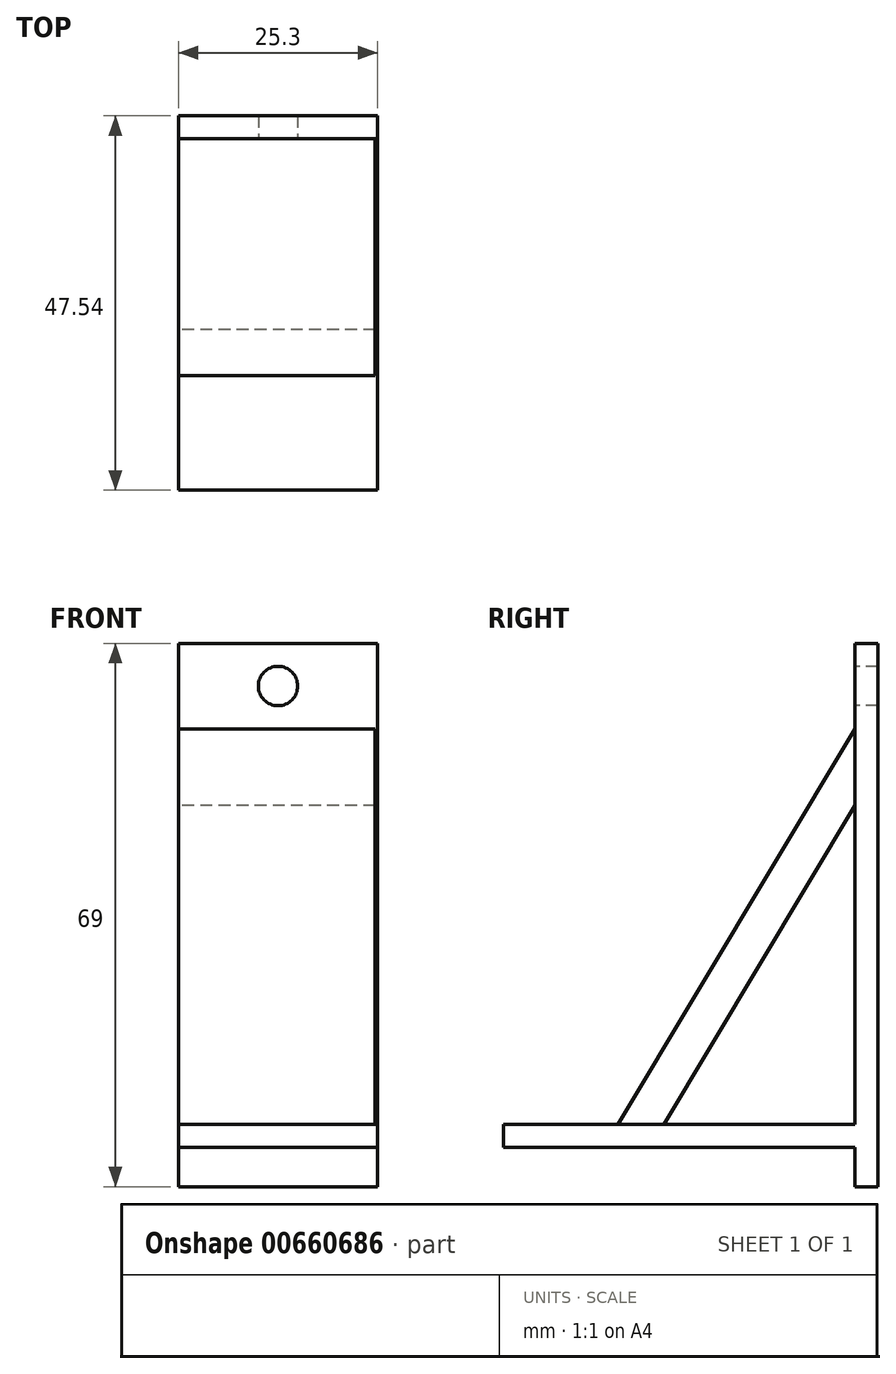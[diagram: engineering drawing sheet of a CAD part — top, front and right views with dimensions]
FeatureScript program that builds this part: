
annotation { "Feature Type Name" : "Feature", "Feature Type Description" : "" }
export const myFeature = defineFeature(function(context is Context, id is Id, definition is map)
    precondition{}
    {
        {
            var Q0;
            Q0=qCreatedBy(makeId("Front.planeOp"),FACE);
            var sketch = newSketch(context, id + "F0", { "sketchPlane" : qUnion([Q0])});
            skLineSegment(sketch, "E0.bottom", {"start": v(-12.65, 34.5) * mm, "end": v(12.66, 34.5) * mm});
            skLineSegment(sketch, "E0.top", {"start": v(-12.66, -34.5) * mm, "end": v(12.65, -34.5) * mm});
            skLineSegment(sketch, "E0.left", {"start": v(-12.65, 34.5) * mm, "end": v(-12.66, -34.5) * mm});
            skLineSegment(sketch, "E0.right", {"start": v(12.66, 34.5) * mm, "end": v(12.65, -34.5) * mm});
            skPoint(sketch, "E0.middle", {"position": v(0, 0) * mm});
            skSolve(sketch);
        }
        {
            var Q0;
            Q0 = qSketchRegion(id + "F0", true);
            extrude(context, id + "F1", {"entities" : qUnion([Q0]), "endBound" : BoundingType.SYMMETRIC, "depth" : 2.9 * mm, "offsetDistance" : 25.4 * mm});
        }
        {
            var Q0;
            Q0=makeQuery(id+"F1.opExtrude","CAP_FACE",FACE,{"disambiguationData":[OSD([sQuery(id+"F0.wireOp",EDGE,"E0.bottom"),sQuery(id+"F0.wireOp",EDGE,"E0.top"),sQuery(id+"F0.wireOp",EDGE,"E0.left"),sQuery(id+"F0.wireOp",EDGE,"E0.right")])],"isStart":false});
            var sketch = newSketch(context, id + "F2", { "sketchPlane" : qUnion([Q0])});
            skLineSegment(sketch, "E1", {"start": v(-12.66, -26.6) * mm, "end": v(12.65, -26.6) * mm});
            skLineSegment(sketch, "E2", {"start": v(12.65, -26.6) * mm, "end": v(12.65, -29.5) * mm});
            skLineSegment(sketch, "E3", {"start": v(12.65, -29.5) * mm, "end": v(-12.66, -29.5) * mm});
            skLineSegment(sketch, "E4", {"start": v(-12.66, -29.5) * mm, "end": v(-12.66, -26.6) * mm});
            skSolve(sketch);
        }
        {
            var Q0;
            Q0 = qSketchRegion(id + "F2", true);
            extrude(context, id + "F3", {"entities" : qUnion([Q0]), "operationType" : NewBodyOperationType.ADD, "depth" : 44.64 * mm, "hasOffset" : true, "offsetDistance" : 25.4 * mm});
        }
        {
            var Q0;
            {var subQ0=sQuery(id+"F0.wireOp",EDGE,"E0.left");var subQ1=sQuery(id+"F0.wireOp",EDGE,"E0.right");var subQ2=sQuery(id+"F0.wireOp",EDGE,"E0.bottom");Q0=makeQuery(id+"F3.boolean.opBoolean","SPLIT",FACE,{"disambiguationData":[TD([makeQuery(id+"F1.opExtrude","SWEPT_FACE",FACE,{"disambiguationData":[OSD([subQ2])]})])],"derivedFrom":makeQuery(id+"F1.opExtrude","CAP_FACE",FACE,{"disambiguationData":[OSD([subQ2,sQuery(id+"F0.wireOp",EDGE,"E0.top"),subQ0,subQ1])],"isStart":false})});}
            var sketch = newSketch(context, id + "F4", { "sketchPlane" : qUnion([Q0])});
            skLineSegment(sketch, "E5", {"start": v(-12.65, 23.67) * mm, "end": v(12.66, 23.67) * mm});
            skSolve(sketch);
        }
        {
            var Q0;
            Q0=makeQuery(id+"F3.opExtrude","SWEPT_FACE",FACE,{"disambiguationData":[OSD([sQuery(id+"F2.wireOp",EDGE,"E1")])]});
            var sketch = newSketch(context, id + "F5", { "sketchPlane" : qUnion([Q0])});
            skLineSegment(sketch, "E6", {"start": v(12.65, -31.55) * mm, "end": v(-12.66, -31.55) * mm});
            skSolve(sketch);
        }
        {
            var Q0;
            Q0=sQuery(id+"F5.wireOp",EDGE,"E6");
            var Q1;
            Q1=sQuery(id+"F5.wireOp",VERTEX,"E6.end");
            cPlane(context, id + "F6", {"entities" : qUnion([Q0, Q1]), "cplaneType" : CPlaneType.LINE_POINT, "offset" : 1 * mm, "width" : 150 * mm, "height" : 150 * mm});
        }
        {
            var Q0;
            Q0=qCreatedBy(id+"F6.planeOp",FACE);
            var sketch = newSketch(context, id + "F7", { "sketchPlane" : qUnion([Q0])});
            skLineSegment(sketch, "E7", {"start": v(31.55, -26.6) * mm, "end": v(1.45, 23.67) * mm});
            skLineSegment(sketch, "E8", {"start": v(31.55, -26.6) * mm, "end": v(25.72, -26.6) * mm});
            skLineSegment(sketch, "E9", {"start": v(25.72, -26.6) * mm, "end": v(1.45, 13.94) * mm});
            skLineSegment(sketch, "E10", {"start": v(1.45, 13.94) * mm, "end": v(1.45, 23.67) * mm});
            skSolve(sketch);
        }
        {
            var Q0;
            Q0 = qSketchRegion(id + "F7", true);
            extrude(context, id + "F8", {"entities" : qUnion([Q0]), "operationType" : NewBodyOperationType.ADD, "oppositeDirection" : true, "depth" : 25 * mm, "offsetDistance" : 25 * mm});
        }
        {
            var Q0;
            {var subQ0=sQuery(id+"F4.wireOp",EDGE,"E5");Q0=makeQuery(id+"F4.imprint","IMPRINT",FACE,{"disambiguationData":[TD([[makeQuery(id+"F4.imprint","IMPRINT",EDGE,{"derivedFrom":subQ0}),1.0]])]});}
            var sketch = newSketch(context, id + "F9", { "sketchPlane" : qUnion([Q0])});
            skCircle(sketch, "E11", {"center": v(0, 29.1) * mm, "radius": 2.35 * mm});
            skSolve(sketch);
        }
        {
            var Q0;
            Q0=sQuery(id+"F9.wireOp",VERTEX,"E11.center");
            var Q1;
            Q1=makeQuery(id+"F1.opExtrude","SWEPT_BODY",BODY,{"disambiguationData":[OSD([sQuery(id+"F0.wireOp",EDGE,"E0.bottom"),sQuery(id+"F0.wireOp",EDGE,"E0.top"),sQuery(id+"F0.wireOp",EDGE,"E0.left"),sQuery(id+"F0.wireOp",EDGE,"E0.right")])]});
            hole(context, id + "F10", {"style" : HoleStyle.SIMPLE, "endStyle" : HoleEndStyle.THROUGH, "holeDiameter" : 5 * mm, "majorDiameter" : 6.35 * mm, "isTappedThrough" : true, "tappedDepth" : 12 * mm, "tapClearance" : 3, "locations" : qUnion([Q0]), "scope" : qUnion([Q1])});
        }
    });
